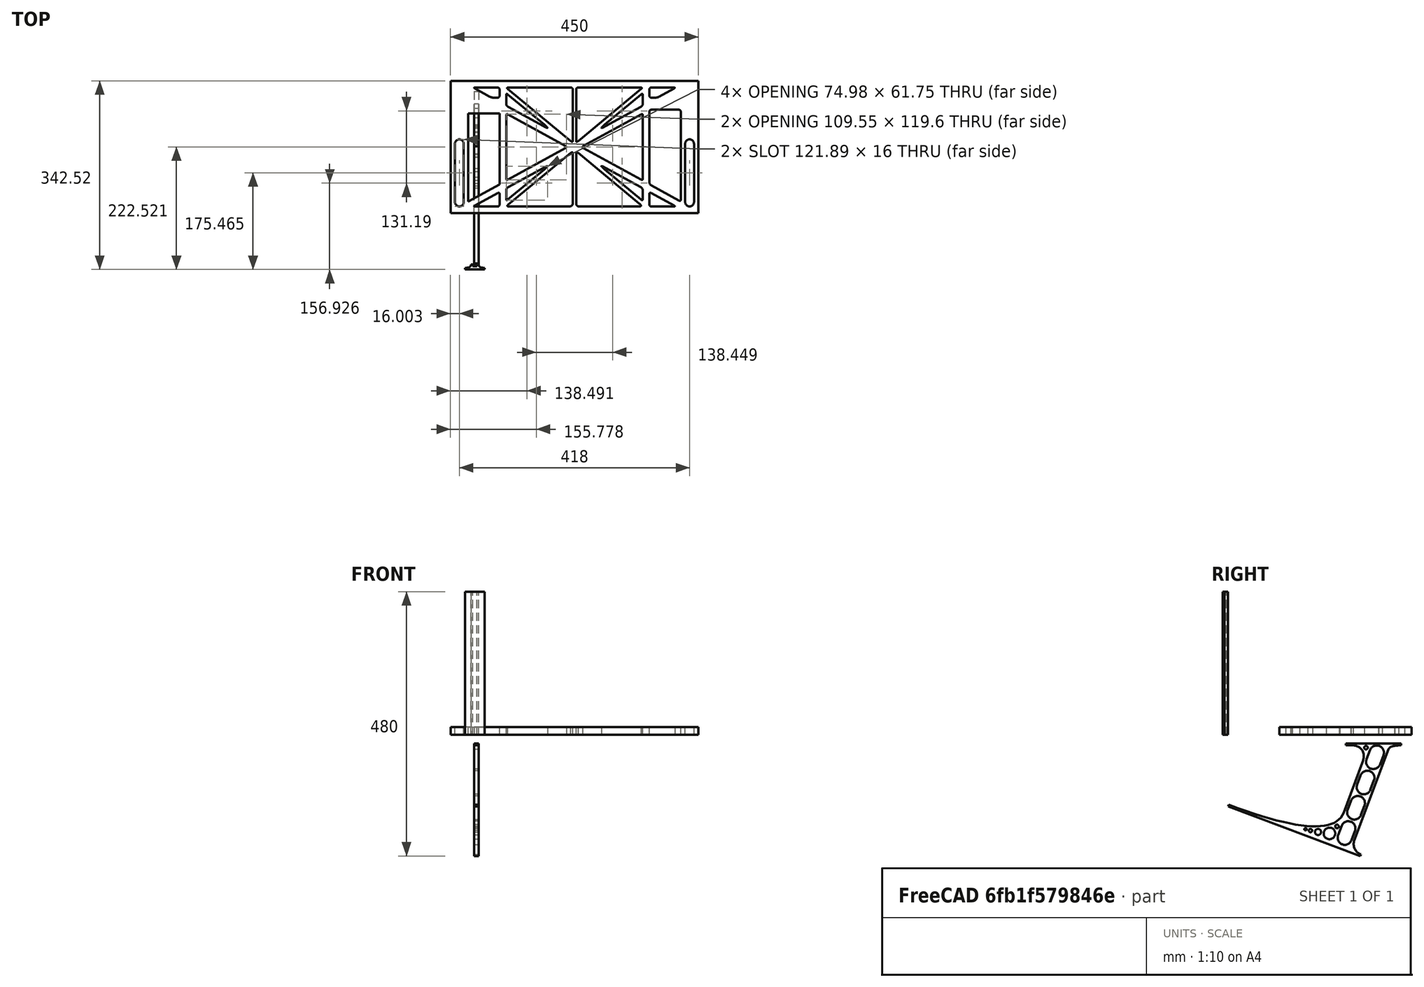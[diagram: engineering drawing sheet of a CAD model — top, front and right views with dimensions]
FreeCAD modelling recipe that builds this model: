
FCSTD DOCUMENT  (FreeCAD 0.19R0.19.2)
Label: laptopStand126FCStd
License: All rights reserved
LicenseURL: http://en.wikipedia.org/wiki/All_rights_reserved
objects: Sketcher::SketchObject×3, Part::Extrusion×3
note: 6 computed .brp shape members not serialized (recipe doc carries the construction recipe); baked Part::Feature solids carry a one-line shape summary decoded from their .brp

FEATURE [Sketcher::SketchObject] Sketch
  FullyConstrained = false
  sketch-geometry (352):
    g0: LineSegment StartX=-10.9272 StartY=-82.7794 StartZ=0 EndX=46.0728 EndY=-51.4823 EndZ=0
    g1: LineSegment StartX=-10.9272 StartY=76.4095 StartZ=0 EndX=-10.9272 EndY=-82.7794 EndZ=0
    g2: LineSegment StartX=46.0728 StartY=76.4095 StartZ=0 EndX=46.0728 EndY=-51.4823 EndZ=0
    g3: LineSegment StartX=-42.9272 StartY=136.221 StartZ=0 EndX=-42.9272 EndY=-103.779 EndZ=0
    g4: LineSegment StartX=407.073 StartY=136.221 StartZ=0 EndX=407.073 EndY=-103.779 EndZ=0
    g5: ArcOfCircle CenterX=-26.9272 CenterY=22.1087 CenterZ=0 NormalX=0 NormalY=0 NormalZ=1 AngleXU=0 Radius=8 StartAngle=1e-16 EndAngle=3.14159
    g6: ArcOfCircle CenterX=-26.9272 CenterY=-83.7794 CenterZ=0 NormalX=0 NormalY=0 NormalZ=1 AngleXU=0 Radius=8 StartAngle=3.14159 EndAngle=6.28319
    g7: LineSegment StartX=-34.9272 StartY=22.1087 StartZ=0 EndX=-34.9272 EndY=-83.7794 EndZ=0
    g8: LineSegment StartX=-18.9272 StartY=22.1087 StartZ=0 EndX=-18.9272 EndY=-83.7794 EndZ=0
    g9: ArcOfCircle CenterX=391.073 CenterY=22.1087 CenterZ=0 NormalX=0 NormalY=0 NormalZ=1 AngleXU=0 Radius=8 StartAngle=-4.4e-15 EndAngle=3.14159
    g10: LineSegment StartX=399.073 StartY=22.1087 StartZ=0 EndX=399.073 EndY=-83.7794 EndZ=0
    g11: LineSegment StartX=383.073 StartY=22.1087 StartZ=0 EndX=383.073 EndY=-83.7794 EndZ=0
    g12: ArcOfCircle CenterX=391.073 CenterY=-83.7794 CenterZ=0 NormalX=0 NormalY=0 NormalZ=1 AngleXU=0 Radius=8 StartAngle=3.14159 EndAngle=6.28319
    g13: Circle CenterX=175.022 CenterY=27.0628 CenterZ=0 NormalX=0 NormalY=0 NormalZ=1 AngleXU=0 Radius=1
    g14: Circle CenterX=179.022 CenterY=24.8665 CenterZ=0 NormalX=0 NormalY=0 NormalZ=1 AngleXU=0 Radius=1
    g15: Circle CenterX=179.022 CenterY=27.0628 CenterZ=0 NormalX=0 NormalY=0 NormalZ=1 AngleXU=0 Radius=1
    g16: BSplineCurve PolesCount=3 KnotsCount=2 Degree=2 IsPeriodic=0
    g17: GeomPoint X=175.022 Y=27.0628 Z=0
    g18: GeomPoint X=179.022 Y=27.0628 Z=0
    g19: Circle CenterX=189.124 CenterY=27.0628 CenterZ=0 NormalX=0 NormalY=0 NormalZ=1 AngleXU=0 Radius=1
    g20: Circle CenterX=185.124 CenterY=24.8665 CenterZ=0 NormalX=0 NormalY=0 NormalZ=1 AngleXU=0 Radius=1
    g21: Circle CenterX=185.124 CenterY=27.0628 CenterZ=0 NormalX=0 NormalY=0 NormalZ=1 AngleXU=0 Radius=1
    g22: BSplineCurve PolesCount=3 KnotsCount=2 Degree=2 IsPeriodic=0
    g23: GeomPoint X=189.124 Y=27.0628 Z=0
    g24: GeomPoint X=185.124 Y=27.0628 Z=0
    g25: Circle CenterX=175.022 CenterY=5.37834 CenterZ=0 NormalX=0 NormalY=0 NormalZ=1 AngleXU=0 Radius=1
    g26: Circle CenterX=179.022 CenterY=7.57463 CenterZ=0 NormalX=0 NormalY=0 NormalZ=1 AngleXU=0 Radius=1
    g27: Circle CenterX=179.022 CenterY=5.34704 CenterZ=0 NormalX=0 NormalY=0 NormalZ=1 AngleXU=0 Radius=1
    g28: BSplineCurve PolesCount=3 KnotsCount=2 Degree=2 IsPeriodic=0
    g29: GeomPoint X=175.022 Y=5.37834 Z=0
    g30: GeomPoint X=179.022 Y=5.34704 Z=0
    g31: Circle CenterX=189.124 CenterY=5.37834 CenterZ=0 NormalX=0 NormalY=0 NormalZ=1 AngleXU=0 Radius=1
    g32: Circle CenterX=185.124 CenterY=7.57463 CenterZ=0 NormalX=0 NormalY=0 NormalZ=1 AngleXU=0 Radius=1
    g33: Circle CenterX=185.124 CenterY=5.34704 CenterZ=0 NormalX=0 NormalY=0 NormalZ=1 AngleXU=0 Radius=1
    g34: BSplineCurve PolesCount=3 KnotsCount=2 Degree=2 IsPeriodic=0
    g35: GeomPoint X=189.124 Y=5.37834 Z=0
    g36: GeomPoint X=185.124 Y=5.34704 Z=0
    g37: Circle CenterX=165.871 CenterY=18.1458 CenterZ=0 NormalX=0 NormalY=0 NormalZ=1 AngleXU=0 Radius=1
    g38: Circle CenterX=169.377 CenterY=16.2206 CenterZ=0 NormalX=0 NormalY=0 NormalZ=1 AngleXU=0 Radius=1
    g39: Circle CenterX=165.871 CenterY=14.2954 CenterZ=0 NormalX=0 NormalY=0 NormalZ=1 AngleXU=0 Radius=1
    g40: BSplineCurve PolesCount=3 KnotsCount=2 Degree=2 IsPeriodic=0
    g41: GeomPoint X=165.871 Y=18.1458 Z=0
    g42: GeomPoint X=165.871 Y=14.2954 Z=0
    g43: Circle CenterX=198.275 CenterY=18.1458 CenterZ=0 NormalX=0 NormalY=0 NormalZ=1 AngleXU=0 Radius=1
    g44: Circle CenterX=194.768 CenterY=16.2206 CenterZ=0 NormalX=0 NormalY=0 NormalZ=1 AngleXU=0 Radius=1
    g45: Circle CenterX=198.275 CenterY=14.2954 CenterZ=0 NormalX=0 NormalY=0 NormalZ=1 AngleXU=0 Radius=1
    g46: BSplineCurve PolesCount=3 KnotsCount=2 Degree=2 IsPeriodic=0
    g47: GeomPoint X=198.275 Y=18.1458 Z=0
    g48: GeomPoint X=198.275 Y=14.2954 Z=0
    g49: LineSegment StartX=407.073 StartY=-103.779 StartZ=0 EndX=-42.9272 EndY=-103.779 EndZ=0
    g50: LineSegment StartX=407.073 StartY=136.221 StartZ=0 EndX=-42.9272 EndY=136.221 EndZ=0
    g51: LineSegment StartX=46.0728 StartY=76.4095 StartZ=0 EndX=-10.9272 EndY=76.4095 EndZ=0
    g52: Circle CenterX=125.607 CenterY=54.1951 CenterZ=0 NormalX=0 NormalY=0 NormalZ=1 AngleXU=0 Radius=1
    g53: Circle CenterX=139.632 CenterY=46.4944 CenterZ=0 NormalX=0 NormalY=0 NormalZ=1 AngleXU=0 Radius=1
    g54: Circle CenterX=127.326 CenterY=56.7187 CenterZ=0 NormalX=0 NormalY=0 NormalZ=1 AngleXU=0 Radius=1
    g55: BSplineCurve PolesCount=3 KnotsCount=2 Degree=2 IsPeriodic=0
    g56: GeomPoint X=125.607 Y=54.1951 Z=0
    g57: GeomPoint X=127.326 Y=56.7187 Z=0
    g58: Circle CenterX=236.821 CenterY=56.7187 CenterZ=0 NormalX=0 NormalY=0 NormalZ=1 AngleXU=0 Radius=1
    g59: Circle CenterX=224.513 CenterY=46.4944 CenterZ=0 NormalX=0 NormalY=0 NormalZ=1 AngleXU=0 Radius=1
    g60: Circle CenterX=238.538 CenterY=54.1951 CenterZ=0 NormalX=0 NormalY=0 NormalZ=1 AngleXU=0 Radius=1
    g61: BSplineCurve PolesCount=3 KnotsCount=2 Degree=2 IsPeriodic=0
    g62: GeomPoint X=236.821 Y=56.7187 Z=0
    g63: GeomPoint X=238.538 Y=54.1951 Z=0
    g64: Circle CenterX=238.538 CenterY=-21.7539 CenterZ=0 NormalX=0 NormalY=0 NormalZ=1 AngleXU=0 Radius=1
    g65: Circle CenterX=224.513 CenterY=-14.0532 CenterZ=0 NormalX=0 NormalY=0 NormalZ=1 AngleXU=0 Radius=1
    g66: Circle CenterX=236.821 CenterY=-24.2775 CenterZ=0 NormalX=0 NormalY=0 NormalZ=1 AngleXU=0 Radius=1
    g67: BSplineCurve PolesCount=3 KnotsCount=2 Degree=2 IsPeriodic=0
    g68: GeomPoint X=238.538 Y=-21.7539 Z=0
    g69: GeomPoint X=236.821 Y=-24.2775 Z=0
    g70: Circle CenterX=125.607 CenterY=-21.7539 CenterZ=0 NormalX=0 NormalY=0 NormalZ=1 AngleXU=0 Radius=1
    g71: Circle CenterX=139.632 CenterY=-14.0532 CenterZ=0 NormalX=0 NormalY=0 NormalZ=1 AngleXU=0 Radius=1
    g72: Circle CenterX=127.325 CenterY=-24.2775 CenterZ=0 NormalX=0 NormalY=0 NormalZ=1 AngleXU=0 Radius=1
    g73: BSplineCurve PolesCount=3 KnotsCount=2 Degree=2 IsPeriodic=0
    g74: GeomPoint X=125.607 Y=-21.7539 Z=0
    g75: GeomPoint X=127.325 Y=-24.2775 Z=0
    g76: Circle CenterX=302.996 CenterY=111.695 CenterZ=0 NormalX=0 NormalY=0 NormalZ=1 AngleXU=0 Radius=1
    g77: Circle CenterX=306.073 CenterY=114.251 CenterZ=0 NormalX=0 NormalY=0 NormalZ=1 AngleXU=0 Radius=1
    g78: Circle CenterX=306.073 CenterY=110.251 CenterZ=0 NormalX=0 NormalY=0 NormalZ=1 AngleXU=0 Radius=1
    g79: BSplineCurve PolesCount=3 KnotsCount=2 Degree=2 IsPeriodic=0
    g80: GeomPoint X=302.996 Y=111.695 Z=0
    g81: GeomPoint X=306.073 Y=110.251 Z=0
    g82: Circle CenterX=306.073 CenterY=95.2763 CenterZ=0 NormalX=0 NormalY=0 NormalZ=1 AngleXU=0 Radius=1
    g83: Circle CenterX=306.073 CenterY=91.2763 CenterZ=0 NormalX=0 NormalY=0 NormalZ=1 AngleXU=0 Radius=1
    g84: Circle CenterX=302.567 CenterY=89.3511 CenterZ=0 NormalX=0 NormalY=0 NormalZ=1 AngleXU=0 Radius=1
    g85: BSplineCurve PolesCount=3 KnotsCount=2 Degree=2 IsPeriodic=0
    g86: GeomPoint X=306.073 Y=95.2763 Z=0
    g87: GeomPoint X=302.567 Y=89.3511 Z=0
    g88: LineSegment StartX=306.073 StartY=110.251 StartZ=0 EndX=306.073 EndY=95.2763 EndZ=0
    g89: LineSegment StartX=302.996 StartY=111.695 StartZ=0 EndX=236.821 EndY=56.7187 EndZ=0
    g90: LineSegment StartX=238.538 StartY=54.1951 StartZ=0 EndX=302.567 EndY=89.3511 EndZ=0
    g91: Circle CenterX=61.1496 CenterY=111.695 CenterZ=0 NormalX=0 NormalY=0 NormalZ=1 AngleXU=0 Radius=1
    g92: Circle CenterX=58.0728 CenterY=114.251 CenterZ=0 NormalX=0 NormalY=0 NormalZ=1 AngleXU=0 Radius=1
    g93: Circle CenterX=58.0728 CenterY=110.251 CenterZ=0 NormalX=0 NormalY=0 NormalZ=1 AngleXU=0 Radius=1
    g94: BSplineCurve PolesCount=3 KnotsCount=2 Degree=2 IsPeriodic=0
    g95: GeomPoint X=61.1496 Y=111.695 Z=0
    g96: GeomPoint X=58.0728 Y=110.251 Z=0
    g97: Circle CenterX=61.5791 CenterY=89.3511 CenterZ=0 NormalX=0 NormalY=0 NormalZ=1 AngleXU=0 Radius=1
    g98: Circle CenterX=58.0728 CenterY=91.2763 CenterZ=0 NormalX=0 NormalY=0 NormalZ=1 AngleXU=0 Radius=1
    g99: Circle CenterX=58.0728 CenterY=95.2763 CenterZ=0 NormalX=0 NormalY=0 NormalZ=1 AngleXU=0 Radius=1
    g100: BSplineCurve PolesCount=3 KnotsCount=2 Degree=2 IsPeriodic=0
    g101: GeomPoint X=61.5791 Y=89.3511 Z=0
    g102: GeomPoint X=58.0728 Y=95.2763 Z=0
    g103: LineSegment StartX=58.0728 StartY=110.251 StartZ=0 EndX=58.0728 EndY=95.2763 EndZ=0
    g104: LineSegment StartX=61.1496 StartY=111.695 StartZ=0 EndX=127.326 EndY=56.7187 EndZ=0
    g105: LineSegment StartX=125.607 StartY=54.1951 StartZ=0 EndX=61.5791 EndY=89.3511 EndZ=0
    g106: Circle CenterX=61.5791 CenterY=-56.9099 CenterZ=0 NormalX=0 NormalY=0 NormalZ=1 AngleXU=0 Radius=1
    g107: Circle CenterX=58.0728 CenterY=-58.8351 CenterZ=0 NormalX=0 NormalY=0 NormalZ=1 AngleXU=0 Radius=1
    g108: Circle CenterX=58.0728 CenterY=-62.8351 CenterZ=0 NormalX=0 NormalY=0 NormalZ=1 AngleXU=0 Radius=1
    g109: BSplineCurve PolesCount=3 KnotsCount=2 Degree=2 IsPeriodic=0
    g110: GeomPoint X=61.5791 Y=-56.9099 Z=0
    g111: GeomPoint X=58.0728 Y=-62.8351 Z=0
    g112: Circle CenterX=58.0728 CenterY=-77.8102 CenterZ=0 NormalX=0 NormalY=0 NormalZ=1 AngleXU=0 Radius=1
    g113: Circle CenterX=58.0728 CenterY=-81.8102 CenterZ=0 NormalX=0 NormalY=0 NormalZ=1 AngleXU=0 Radius=1
    g114: Circle CenterX=61.1496 CenterY=-79.2541 CenterZ=0 NormalX=0 NormalY=0 NormalZ=1 AngleXU=0 Radius=1
    g115: BSplineCurve PolesCount=3 KnotsCount=2 Degree=2 IsPeriodic=0
    g116: GeomPoint X=58.0728 Y=-77.8102 Z=0
    g117: GeomPoint X=61.1496 Y=-79.2541 Z=0
    g118: LineSegment StartX=58.0728 StartY=-62.8351 StartZ=0 EndX=58.0728 EndY=-77.8102 EndZ=0
    g119: LineSegment StartX=61.1496 StartY=-79.2541 StartZ=0 EndX=127.325 EndY=-24.2775 EndZ=0
    g120: LineSegment StartX=125.607 StartY=-21.7539 StartZ=0 EndX=61.5791 EndY=-56.9099 EndZ=0
    g121: Circle CenterX=302.567 CenterY=-56.9099 CenterZ=0 NormalX=0 NormalY=0 NormalZ=1 AngleXU=0 Radius=1
    g122: Circle CenterX=306.073 CenterY=-58.8351 CenterZ=0 NormalX=0 NormalY=0 NormalZ=1 AngleXU=0 Radius=1
    g123: Circle CenterX=306.073 CenterY=-62.8351 CenterZ=0 NormalX=0 NormalY=0 NormalZ=1 AngleXU=0 Radius=1
    g124: BSplineCurve PolesCount=3 KnotsCount=2 Degree=2 IsPeriodic=0
    g125: GeomPoint X=302.567 Y=-56.9099 Z=0
    g126: GeomPoint X=306.073 Y=-62.8351 Z=0
    g127: Circle CenterX=302.996 CenterY=-79.2541 CenterZ=0 NormalX=0 NormalY=0 NormalZ=1 AngleXU=0 Radius=1
    g128: Circle CenterX=306.073 CenterY=-81.8102 CenterZ=0 NormalX=0 NormalY=0 NormalZ=1 AngleXU=0 Radius=1
    g129: Circle CenterX=306.073 CenterY=-77.8102 CenterZ=0 NormalX=0 NormalY=0 NormalZ=1 AngleXU=0 Radius=1
    g130: BSplineCurve PolesCount=3 KnotsCount=2 Degree=2 IsPeriodic=0
    g131: GeomPoint X=302.996 Y=-79.2541 Z=0
    g132: GeomPoint X=306.073 Y=-77.8102 Z=0
    g133: LineSegment StartX=306.073 StartY=-62.8351 StartZ=0 EndX=306.073 EndY=-77.8102 EndZ=0
    g134: LineSegment StartX=302.996 StartY=-79.2541 StartZ=0 EndX=236.821 EndY=-24.2775 EndZ=0
    g135: LineSegment StartX=238.538 StartY=-21.7539 StartZ=0 EndX=302.567 EndY=-56.9099 EndZ=0
    g136: Circle CenterX=61.6457 CenterY=-88.8112 CenterZ=0 NormalX=0 NormalY=0 NormalZ=1 AngleXU=0 Radius=1
    g137: Circle CenterX=58.0728 CenterY=-91.7794 CenterZ=0 NormalX=0 NormalY=0 NormalZ=1 AngleXU=0 Radius=1
    g138: Circle CenterX=63.9135 CenterY=-91.7794 CenterZ=0 NormalX=0 NormalY=0 NormalZ=1 AngleXU=0 Radius=1
    g139: BSplineCurve PolesCount=3 KnotsCount=2 Degree=2 IsPeriodic=0
    g140: GeomPoint X=61.6457 Y=-88.8112 Z=0
    g141: GeomPoint X=63.9135 Y=-91.7794 Z=0
    g142: Circle CenterX=179.022 CenterY=-85.8163 CenterZ=0 NormalX=0 NormalY=0 NormalZ=1 AngleXU=0 Radius=1
    g143: Circle CenterX=179.022 CenterY=-91.7794 CenterZ=0 NormalX=0 NormalY=0 NormalZ=1 AngleXU=0 Radius=1
    g144: Circle CenterX=171.895 CenterY=-91.7794 CenterZ=0 NormalX=0 NormalY=0 NormalZ=1 AngleXU=0 Radius=1
    g145: BSplineCurve PolesCount=3 KnotsCount=2 Degree=2 IsPeriodic=0
    g146: GeomPoint X=179.022 Y=-85.8163 Z=0
    g147: GeomPoint X=171.895 Y=-91.7794 Z=0
    g148: Circle CenterX=185.124 CenterY=-86.2028 CenterZ=0 NormalX=0 NormalY=0 NormalZ=1 AngleXU=0 Radius=1
    g149: Circle CenterX=185.124 CenterY=-91.7794 CenterZ=0 NormalX=0 NormalY=0 NormalZ=1 AngleXU=0 Radius=1
    g150: Circle CenterX=191.747 CenterY=-91.7794 CenterZ=0 NormalX=0 NormalY=0 NormalZ=1 AngleXU=0 Radius=1
    g151: BSplineCurve PolesCount=3 KnotsCount=2 Degree=2 IsPeriodic=0
    g152: GeomPoint X=185.124 Y=-86.2028 Z=0
    g153: GeomPoint X=191.747 Y=-91.7794 Z=0
    g154: Circle CenterX=299.888 CenterY=-86.6413 CenterZ=0 NormalX=0 NormalY=0 NormalZ=1 AngleXU=0 Radius=1
    g155: Circle CenterX=306.073 CenterY=-91.7794 CenterZ=0 NormalX=0 NormalY=0 NormalZ=1 AngleXU=0 Radius=1
    g156: Circle CenterX=298.776 CenterY=-91.7794 CenterZ=0 NormalX=0 NormalY=0 NormalZ=1 AngleXU=0 Radius=1
    g157: BSplineCurve PolesCount=3 KnotsCount=2 Degree=2 IsPeriodic=0
    g158: GeomPoint X=299.888 Y=-86.6413 Z=0
    g159: GeomPoint X=298.776 Y=-91.7794 Z=0
    g160: LineSegment StartX=189.124 StartY=5.37834 StartZ=0 EndX=299.888 EndY=-86.6413 EndZ=0
    g161: LineSegment StartX=298.776 StartY=-91.7794 StartZ=0 EndX=191.747 EndY=-91.7794 EndZ=0
    g162: LineSegment StartX=185.124 StartY=-86.2028 StartZ=0 EndX=185.124 EndY=5.34704 EndZ=0
    g163: LineSegment StartX=179.022 StartY=5.34704 StartZ=0 EndX=179.022 EndY=-85.8163 EndZ=0
    g164: LineSegment StartX=171.895 StartY=-91.7794 StartZ=0 EndX=63.9135 EndY=-91.7794 EndZ=0
    g165: LineSegment StartX=61.6457 StartY=-88.8112 StartZ=0 EndX=175.022 EndY=5.37834 EndZ=0
    g166: Circle CenterX=302.073 CenterY=124.221 CenterZ=0 NormalX=0 NormalY=0 NormalZ=1 AngleXU=0 Radius=1
    g167: Circle CenterX=306.073 CenterY=124.221 CenterZ=0 NormalX=0 NormalY=0 NormalZ=1 AngleXU=0 Radius=1
    g168: Circle CenterX=302.996 CenterY=121.665 CenterZ=0 NormalX=0 NormalY=0 NormalZ=1 AngleXU=0 Radius=1
    g169: BSplineCurve PolesCount=3 KnotsCount=2 Degree=2 IsPeriodic=0
    g170: GeomPoint X=302.073 Y=124.221 Z=0
    g171: GeomPoint X=302.996 Y=121.665 Z=0
    g172: Circle CenterX=189.124 CenterY=124.221 CenterZ=0 NormalX=0 NormalY=0 NormalZ=1 AngleXU=0 Radius=1
    g173: Circle CenterX=185.124 CenterY=124.221 CenterZ=0 NormalX=0 NormalY=0 NormalZ=1 AngleXU=0 Radius=1
    g174: Circle CenterX=185.124 CenterY=120.221 CenterZ=0 NormalX=0 NormalY=0 NormalZ=1 AngleXU=0 Radius=1
    g175: BSplineCurve PolesCount=3 KnotsCount=2 Degree=2 IsPeriodic=0
    g176: GeomPoint X=189.124 Y=124.221 Z=0
    g177: GeomPoint X=185.124 Y=120.221 Z=0
    g178: Circle CenterX=175.022 CenterY=124.221 CenterZ=0 NormalX=0 NormalY=0 NormalZ=1 AngleXU=0 Radius=1
    g179: Circle CenterX=179.022 CenterY=124.221 CenterZ=0 NormalX=0 NormalY=0 NormalZ=1 AngleXU=0 Radius=1
    g180: Circle CenterX=179.022 CenterY=120.221 CenterZ=0 NormalX=0 NormalY=0 NormalZ=1 AngleXU=0 Radius=1
    g181: BSplineCurve PolesCount=3 KnotsCount=2 Degree=2 IsPeriodic=0
    g182: GeomPoint X=175.022 Y=124.221 Z=0
    g183: GeomPoint X=179.022 Y=120.221 Z=0
    g184: Circle CenterX=62.0728 CenterY=124.221 CenterZ=0 NormalX=0 NormalY=0 NormalZ=1 AngleXU=0 Radius=1
    g185: Circle CenterX=58.0728 CenterY=124.221 CenterZ=0 NormalX=0 NormalY=0 NormalZ=1 AngleXU=0 Radius=1
    g186: Circle CenterX=61.1496 CenterY=121.665 CenterZ=0 NormalX=0 NormalY=0 NormalZ=1 AngleXU=0 Radius=1
    g187: BSplineCurve PolesCount=3 KnotsCount=2 Degree=2 IsPeriodic=0
    g188: GeomPoint X=62.0728 Y=124.221 Z=0
    g189: GeomPoint X=61.1496 Y=121.665 Z=0
    g190: LineSegment StartX=62.0728 StartY=124.221 StartZ=0 EndX=175.022 EndY=124.221 EndZ=0
    g191: LineSegment StartX=179.022 StartY=120.221 StartZ=0 EndX=179.022 EndY=27.0628 EndZ=0
    g192: LineSegment StartX=185.124 StartY=27.0628 StartZ=0 EndX=185.124 EndY=120.221 EndZ=0
    g193: LineSegment StartX=189.124 StartY=124.221 StartZ=0 EndX=302.073 EndY=124.221 EndZ=0
    g194: LineSegment StartX=302.996 StartY=121.665 StartZ=0 EndX=189.124 EndY=27.0628 EndZ=0
    g195: LineSegment StartX=175.022 StartY=27.0628 StartZ=0 EndX=61.1496 EndY=121.665 EndZ=0
    g196: Circle CenterX=61.5791 CenterY=75.4095 CenterZ=0 NormalX=0 NormalY=0 NormalZ=1 AngleXU=0 Radius=1
    g197: Circle CenterX=58.0728 CenterY=77.3346 CenterZ=0 NormalX=0 NormalY=0 NormalZ=1 AngleXU=0 Radius=1
    g198: Circle CenterX=58.0728 CenterY=73.3346 CenterZ=0 NormalX=0 NormalY=0 NormalZ=1 AngleXU=0 Radius=1
    g199: BSplineCurve PolesCount=3 KnotsCount=2 Degree=2 IsPeriodic=0
    g200: GeomPoint X=61.5791 Y=75.4095 Z=0
    g201: GeomPoint X=58.0728 Y=73.3346 Z=0
    g202: Circle CenterX=58.0728 CenterY=-40.8935 CenterZ=0 NormalX=0 NormalY=0 NormalZ=1 AngleXU=0 Radius=1
    g203: Circle CenterX=58.0728 CenterY=-44.8935 CenterZ=0 NormalX=0 NormalY=0 NormalZ=1 AngleXU=0 Radius=1
    g204: Circle CenterX=61.5791 CenterY=-42.9683 CenterZ=0 NormalX=0 NormalY=0 NormalZ=1 AngleXU=0 Radius=1
    g205: BSplineCurve PolesCount=3 KnotsCount=2 Degree=2 IsPeriodic=0
    g206: GeomPoint X=58.0728 Y=-40.8935 Z=0
    g207: GeomPoint X=61.5791 Y=-42.9683 Z=0
    g208: LineSegment StartX=61.5791 StartY=-42.9683 StartZ=0 EndX=165.871 EndY=14.2954 EndZ=0
    g209: LineSegment StartX=165.871 StartY=18.1458 StartZ=0 EndX=61.5791 EndY=75.4095 EndZ=0
    g210: LineSegment StartX=58.0728 StartY=73.3346 StartZ=0 EndX=58.0728 EndY=-40.8935 EndZ=0
    g211: Circle CenterX=302.567 CenterY=-42.9683 CenterZ=0 NormalX=0 NormalY=0 NormalZ=1 AngleXU=0 Radius=1
    g212: Circle CenterX=306.073 CenterY=-44.8935 CenterZ=0 NormalX=0 NormalY=0 NormalZ=1 AngleXU=0 Radius=1
    g213: Circle CenterX=306.073 CenterY=-40.8935 CenterZ=0 NormalX=0 NormalY=0 NormalZ=1 AngleXU=0 Radius=1
    g214: BSplineCurve PolesCount=3 KnotsCount=2 Degree=2 IsPeriodic=0
    g215: GeomPoint X=302.567 Y=-42.9683 Z=0
    g216: GeomPoint X=306.073 Y=-40.8935 Z=0
    g217: Circle CenterX=306.073 CenterY=73.3346 CenterZ=0 NormalX=0 NormalY=0 NormalZ=1 AngleXU=0 Radius=1
    g218: Circle CenterX=306.073 CenterY=77.3346 CenterZ=0 NormalX=0 NormalY=0 NormalZ=1 AngleXU=0 Radius=1
    g219: Circle CenterX=302.567 CenterY=75.4095 CenterZ=0 NormalX=0 NormalY=0 NormalZ=1 AngleXU=0 Radius=1
    g220: BSplineCurve PolesCount=3 KnotsCount=2 Degree=2 IsPeriodic=0
    g221: GeomPoint X=306.073 Y=73.3346 Z=0
    g222: GeomPoint X=302.567 Y=75.4095 Z=0
    g223: LineSegment StartX=302.567 StartY=-42.9683 StartZ=0 EndX=198.275 EndY=14.2954 EndZ=0
    g224: LineSegment StartX=198.275 StartY=18.1458 StartZ=0 EndX=302.567 EndY=75.4095 EndZ=0
    g225: LineSegment StartX=306.073 StartY=73.3346 StartZ=0 EndX=306.073 EndY=-40.8935 EndZ=0
    g226: LineSegment StartX=322.073 StartY=105.865 StartZ=0 EndX=328.643 EndY=105.865 EndZ=0
    g227: LineSegment StartX=318.073 StartY=120.221 StartZ=0 EndX=318.073 EndY=109.865 EndZ=0
    g228: LineSegment StartX=336.157 StartY=107.779 StartZ=0 EndX=362.567 EndY=122.294 EndZ=0
    g229: Circle CenterX=362.073 CenterY=124.221 CenterZ=0 NormalX=0 NormalY=0 NormalZ=1 AngleXU=0 Radius=1
    g230: Circle CenterX=366.073 CenterY=124.221 CenterZ=0 NormalX=0 NormalY=0 NormalZ=1 AngleXU=0 Radius=1
    g231: Circle CenterX=362.567 CenterY=122.294 CenterZ=0 NormalX=0 NormalY=0 NormalZ=1 AngleXU=0 Radius=1
    g232: BSplineCurve PolesCount=3 KnotsCount=2 Degree=2 IsPeriodic=0
    g233: GeomPoint X=362.073 Y=124.221 Z=0
    g234: GeomPoint X=362.567 Y=122.294 Z=0
    g235: Circle CenterX=322.073 CenterY=124.221 CenterZ=0 NormalX=0 NormalY=0 NormalZ=1 AngleXU=0 Radius=1
    g236: Circle CenterX=318.073 CenterY=124.221 CenterZ=0 NormalX=0 NormalY=0 NormalZ=1 AngleXU=0 Radius=1
    g237: Circle CenterX=318.073 CenterY=120.221 CenterZ=0 NormalX=0 NormalY=0 NormalZ=1 AngleXU=0 Radius=1
    g238: BSplineCurve PolesCount=3 KnotsCount=2 Degree=2 IsPeriodic=0
    g239: GeomPoint X=322.073 Y=124.221 Z=0
    g240: GeomPoint X=318.073 Y=120.221 Z=0
    g241: Circle CenterX=322.073 CenterY=105.865 CenterZ=0 NormalX=0 NormalY=0 NormalZ=1 AngleXU=0 Radius=1
    g242: Circle CenterX=318.073 CenterY=105.865 CenterZ=0 NormalX=0 NormalY=0 NormalZ=1 AngleXU=0 Radius=1
    g243: Circle CenterX=318.073 CenterY=109.865 CenterZ=0 NormalX=0 NormalY=0 NormalZ=1 AngleXU=0 Radius=1
    g244: BSplineCurve PolesCount=3 KnotsCount=2 Degree=2 IsPeriodic=0
    g245: GeomPoint X=322.073 Y=105.865 Z=0
    g246: GeomPoint X=318.073 Y=109.865 Z=0
    g247: Circle CenterX=336.157 CenterY=107.779 CenterZ=0 NormalX=0 NormalY=0 NormalZ=1 AngleXU=0 Radius=1
    g248: Circle CenterX=332.651 CenterY=105.853 CenterZ=0 NormalX=0 NormalY=0 NormalZ=1 AngleXU=0 Radius=1
    g249: Circle CenterX=328.643 CenterY=105.865 CenterZ=0 NormalX=0 NormalY=0 NormalZ=1 AngleXU=0 Radius=1
    g250: BSplineCurve PolesCount=3 KnotsCount=2 Degree=2 IsPeriodic=0
    g251: GeomPoint X=336.157 Y=107.779 Z=0
    g252: GeomPoint X=328.643 Y=105.865 Z=0
    g253: LineSegment StartX=322.073 StartY=124.221 StartZ=0 EndX=362.073 EndY=124.221 EndZ=0
    g254: Circle CenterX=371.567 CenterY=-80.8644 CenterZ=0 NormalX=0 NormalY=0 NormalZ=1 AngleXU=0 Radius=1
    g255: Circle CenterX=375.073 CenterY=-82.7896 CenterZ=0 NormalX=0 NormalY=0 NormalZ=1 AngleXU=0 Radius=1
    g256: Circle CenterX=375.073 CenterY=-78.7896 CenterZ=0 NormalX=0 NormalY=0 NormalZ=1 AngleXU=0 Radius=1
    g257: BSplineCurve PolesCount=3 KnotsCount=2 Degree=2 IsPeriodic=0
    g258: GeomPoint X=371.567 Y=-80.8644 Z=0
    g259: GeomPoint X=375.073 Y=-78.7896 Z=0
    g260: Circle CenterX=321.579 CenterY=-53.4075 CenterZ=0 NormalX=0 NormalY=0 NormalZ=1 AngleXU=0 Radius=1
    g261: Circle CenterX=318.073 CenterY=-51.4823 CenterZ=0 NormalX=0 NormalY=0 NormalZ=1 AngleXU=0 Radius=1
    g262: Circle CenterX=318.073 CenterY=-47.4823 CenterZ=0 NormalX=0 NormalY=0 NormalZ=1 AngleXU=0 Radius=1
    g263: BSplineCurve PolesCount=3 KnotsCount=2 Degree=2 IsPeriodic=0
    g264: GeomPoint X=321.579 Y=-53.4075 Z=0
    g265: GeomPoint X=318.073 Y=-47.4823 Z=0
    g266: Circle CenterX=318.073 CenterY=79.9235 CenterZ=0 NormalX=0 NormalY=0 NormalZ=1 AngleXU=0 Radius=1
    g267: Circle CenterX=318.073 CenterY=83.9235 CenterZ=0 NormalX=0 NormalY=0 NormalZ=1 AngleXU=0 Radius=1
    g268: Circle CenterX=322.073 CenterY=83.9235 CenterZ=0 NormalX=0 NormalY=0 NormalZ=1 AngleXU=0 Radius=1
    g269: BSplineCurve PolesCount=3 KnotsCount=2 Degree=2 IsPeriodic=0
    g270: GeomPoint X=318.073 Y=79.9235 Z=0
    g271: GeomPoint X=322.073 Y=83.9235 Z=0
    g272: Circle CenterX=375.073 CenterY=79.9235 CenterZ=0 NormalX=0 NormalY=0 NormalZ=1 AngleXU=0 Radius=1
    g273: Circle CenterX=375.073 CenterY=83.9235 CenterZ=0 NormalX=0 NormalY=0 NormalZ=1 AngleXU=0 Radius=1
    g274: Circle CenterX=371.073 CenterY=83.9235 CenterZ=0 NormalX=0 NormalY=0 NormalZ=1 AngleXU=0 Radius=1
    g275: BSplineCurve PolesCount=3 KnotsCount=2 Degree=2 IsPeriodic=0
    g276: GeomPoint X=375.073 Y=79.9235 Z=0
    g277: GeomPoint X=371.073 Y=83.9235 Z=0
    g278: LineSegment StartX=322.073 StartY=83.9235 StartZ=0 EndX=371.073 EndY=83.9235 EndZ=0
    g279: LineSegment StartX=375.073 StartY=79.9235 StartZ=0 EndX=375.073 EndY=-78.7896 EndZ=0
    g280: LineSegment StartX=371.567 StartY=-80.8644 StartZ=0 EndX=321.579 EndY=-53.4075 EndZ=0
    g281: LineSegment StartX=318.073 StartY=-47.4823 StartZ=0 EndX=318.073 EndY=79.9235 EndZ=0
    g282: Circle CenterX=321.579 CenterY=-67.3492 CenterZ=0 NormalX=0 NormalY=0 NormalZ=1 AngleXU=0 Radius=1
    g283: Circle CenterX=318.073 CenterY=-65.424 CenterZ=0 NormalX=0 NormalY=0 NormalZ=1 AngleXU=0 Radius=1
    g284: Circle CenterX=318.073 CenterY=-69.424 CenterZ=0 NormalX=0 NormalY=0 NormalZ=1 AngleXU=0 Radius=1
    g285: BSplineCurve PolesCount=3 KnotsCount=2 Degree=2 IsPeriodic=0
    g286: GeomPoint X=321.579 Y=-67.3492 Z=0
    g287: GeomPoint X=318.073 Y=-69.424 Z=0
    g288: Circle CenterX=362.567 CenterY=-89.8542 CenterZ=0 NormalX=0 NormalY=0 NormalZ=1 AngleXU=0 Radius=1
    g289: Circle CenterX=366.073 CenterY=-91.7794 CenterZ=0 NormalX=0 NormalY=0 NormalZ=1 AngleXU=0 Radius=1
    g290: Circle CenterX=362.073 CenterY=-91.7794 CenterZ=0 NormalX=0 NormalY=0 NormalZ=1 AngleXU=0 Radius=1
    g291: BSplineCurve PolesCount=3 KnotsCount=2 Degree=2 IsPeriodic=0
    g292: GeomPoint X=362.567 Y=-89.8542 Z=0
    g293: GeomPoint X=362.073 Y=-91.7794 Z=0
    g294: Circle CenterX=322.073 CenterY=-91.7794 CenterZ=0 NormalX=0 NormalY=0 NormalZ=1 AngleXU=0 Radius=1
    g295: Circle CenterX=318.073 CenterY=-91.7794 CenterZ=0 NormalX=0 NormalY=0 NormalZ=1 AngleXU=0 Radius=1
    g296: Circle CenterX=318.073 CenterY=-87.7794 CenterZ=0 NormalX=0 NormalY=0 NormalZ=1 AngleXU=0 Radius=1
    g297: BSplineCurve PolesCount=3 KnotsCount=2 Degree=2 IsPeriodic=0
    g298: GeomPoint X=322.073 Y=-91.7794 Z=0
    g299: GeomPoint X=318.073 Y=-87.7794 Z=0
    g300: LineSegment StartX=362.567 StartY=-89.8542 StartZ=0 EndX=321.579 EndY=-67.3492 EndZ=0
    g301: LineSegment StartX=318.073 StartY=-69.424 StartZ=0 EndX=318.073 EndY=-87.7794 EndZ=0
    g302: LineSegment StartX=322.073 StartY=-91.7794 StartZ=0 EndX=362.073 EndY=-91.7794 EndZ=0
    g303: Circle CenterX=2.07281 CenterY=124.221 CenterZ=0 NormalX=0 NormalY=0 NormalZ=1 AngleXU=0 Radius=1
    g304: Circle CenterX=1.57905 CenterY=122.295 CenterZ=0 NormalX=0 NormalY=0 NormalZ=1 AngleXU=0 Radius=1
    g305: BSplineCurve PolesCount=3 KnotsCount=2 Degree=2 IsPeriodic=0
    g306: GeomPoint X=2.07281 Y=124.221 Z=0
    g307: GeomPoint X=1.57905 Y=122.295 Z=0
    g308: Circle CenterX=42.0728 CenterY=124.221 CenterZ=0 NormalX=0 NormalY=0 NormalZ=1 AngleXU=0 Radius=1
    g309: Circle CenterX=46.0728 CenterY=124.221 CenterZ=0 NormalX=0 NormalY=0 NormalZ=1 AngleXU=0 Radius=1
    g310: Circle CenterX=46.0728 CenterY=120.221 CenterZ=0 NormalX=0 NormalY=0 NormalZ=1 AngleXU=0 Radius=1
    g311: BSplineCurve PolesCount=3 KnotsCount=2 Degree=2 IsPeriodic=0
    g312: GeomPoint X=42.0728 Y=124.221 Z=0
    g313: GeomPoint X=46.0728 Y=120.221 Z=0
    g314: Circle CenterX=46.0728 CenterY=109.865 CenterZ=0 NormalX=0 NormalY=0 NormalZ=1 AngleXU=0 Radius=1
    g315: Circle CenterX=46.0728 CenterY=105.865 CenterZ=0 NormalX=0 NormalY=0 NormalZ=1 AngleXU=0 Radius=1
    g316: Circle CenterX=42.0728 CenterY=105.865 CenterZ=0 NormalX=0 NormalY=0 NormalZ=1 AngleXU=0 Radius=1
    g317: BSplineCurve PolesCount=3 KnotsCount=2 Degree=2 IsPeriodic=0
    g318: GeomPoint X=46.0728 Y=109.865 Z=0
    g319: GeomPoint X=42.0728 Y=105.865 Z=0
    g320: Circle CenterX=35.5028 CenterY=105.865 CenterZ=0 NormalX=0 NormalY=0 NormalZ=1 AngleXU=0 Radius=1
    g321: Circle CenterX=31.5028 CenterY=105.865 CenterZ=0 NormalX=0 NormalY=0 NormalZ=1 AngleXU=0 Radius=1
    g322: Circle CenterX=27.9965 CenterY=107.79 CenterZ=0 NormalX=0 NormalY=0 NormalZ=1 AngleXU=0 Radius=1
    g323: BSplineCurve PolesCount=3 KnotsCount=2 Degree=2 IsPeriodic=0
    g324: GeomPoint X=35.5028 Y=105.865 Z=0
    g325: GeomPoint X=27.9965 Y=107.79 Z=0
    g326: LineSegment StartX=2.07281 StartY=124.221 StartZ=0 EndX=42.0728 EndY=124.221 EndZ=0
    g327: LineSegment StartX=46.0728 StartY=120.221 StartZ=0 EndX=46.0728 EndY=109.865 EndZ=0
    g328: LineSegment StartX=42.0728 StartY=105.865 StartZ=0 EndX=35.5028 EndY=105.865 EndZ=0
    g329: LineSegment StartX=27.9965 StartY=107.79 StartZ=0 EndX=1.57905 EndY=122.295 EndZ=0
    g330: Circle CenterX=42.5666 CenterY=-67.3492 CenterZ=0 NormalX=0 NormalY=0 NormalZ=1 AngleXU=0 Radius=1
    g331: Circle CenterX=46.0728 CenterY=-65.424 CenterZ=0 NormalX=0 NormalY=0 NormalZ=1 AngleXU=0 Radius=1
    g332: Circle CenterX=46.0728 CenterY=-69.424 CenterZ=0 NormalX=0 NormalY=0 NormalZ=1 AngleXU=0 Radius=1
    g333: BSplineCurve PolesCount=3 KnotsCount=2 Degree=2 IsPeriodic=0
    g334: GeomPoint X=42.5666 Y=-67.3492 Z=0
    g335: GeomPoint X=46.0728 Y=-69.424 Z=0
    g336: Circle CenterX=46.0728 CenterY=-87.7794 CenterZ=0 NormalX=0 NormalY=0 NormalZ=1 AngleXU=0 Radius=1
    g337: Circle CenterX=46.0728 CenterY=-91.7794 CenterZ=0 NormalX=0 NormalY=0 NormalZ=1 AngleXU=0 Radius=1
    g338: Circle CenterX=42.0728 CenterY=-91.7794 CenterZ=0 NormalX=0 NormalY=0 NormalZ=1 AngleXU=0 Radius=1
    g339: BSplineCurve PolesCount=3 KnotsCount=2 Degree=2 IsPeriodic=0
    g340: GeomPoint X=46.0728 Y=-87.7794 Z=0
    g341: GeomPoint X=42.0728 Y=-91.7794 Z=0
    g342: Circle CenterX=2.07281 CenterY=-91.7794 CenterZ=0 NormalX=0 NormalY=0 NormalZ=1 AngleXU=0 Radius=1
    g343: Circle CenterX=-1.92719 CenterY=-91.7794 CenterZ=0 NormalX=0 NormalY=0 NormalZ=1 AngleXU=0 Radius=1
    g344: Circle CenterX=1.57905 CenterY=-89.8542 CenterZ=0 NormalX=0 NormalY=0 NormalZ=1 AngleXU=0 Radius=1
    g345: BSplineCurve PolesCount=3 KnotsCount=2 Degree=2 IsPeriodic=0
    g346: GeomPoint X=2.07281 Y=-91.7794 Z=0
    g347: GeomPoint X=1.57905 Y=-89.8542 Z=0
    g348: LineSegment StartX=2.07281 StartY=-91.7794 StartZ=0 EndX=42.0728 EndY=-91.7794 EndZ=0
    g349: LineSegment StartX=46.0728 StartY=-87.7794 StartZ=0 EndX=46.0728 EndY=-69.424 EndZ=0
    g350: LineSegment StartX=42.5666 StartY=-67.3492 StartZ=0 EndX=1.57905 EndY=-89.8542 EndZ=0
    g351: LineSegment StartX=46.0728 StartY=76.4095 StartZ=0 EndX=421.682 EndY=76.4095 EndZ=0
  constraints (585):
    c: Coincident(g0,g2)
    c: Block(g0)
    c: Block(g1)
    c: Vertical(g3)
    c: Vertical(g4)
    c: Block(g4)
    c: Block(g3)
    c: Tangent(g5,g8) = 1.5708
    c: Tangent(g5,g7) = -1.5708
    c: Tangent(g7,g6) = -1.5708
    c: Tangent(g8,g6) = 1.5708
    c: Vertical(g7)
    c: Equal(g5,g6)
    c: Block(g8)
    c: Block(g7)
    c: Tangent(g9,g10) = 1.5708
    c: Tangent(g10,g12) = 1.5708
    c: Equal(g9,g12)
    c: Coincident(g11,g9)
    c: Coincident(g11,g12)
    c: Block(g10)
    c: Block(g11)
    c: Weight(g13) = 1
    c: Equal(g13,g14)
    c: Equal(g13,g15)
    c: InternalAlignment(g13,g16)
    c: InternalAlignment(g14,g16)
    c: InternalAlignment(g15,g16)
    c: InternalAlignment(g17,g16)
    c: InternalAlignment(g18,g16)
    c: Weight(g19) = 1
    c: Equal(g19,g20)
    c: Equal(g19,g21)
    c: InternalAlignment(g19,g22)
    c: InternalAlignment(g20,g22)
    c: InternalAlignment(g21,g22)
    c: InternalAlignment(g23,g22)
    c: InternalAlignment(g24,g22)
    c: Block(g22)
    c: Block(g16)
    c: Weight(g25) = 1
    c: Equal(g25,g26)
    c: Equal(g25,g27)
    c: InternalAlignment(g25,g28)
    c: InternalAlignment(g26,g28)
    c: InternalAlignment(g27,g28)
    c: InternalAlignment(g29,g28)
    c: InternalAlignment(g30,g28)
    c: Weight(g31) = 1
    c: Equal(g31,g32)
    c: Equal(g31,g33)
    c: InternalAlignment(g31,g34)
    c: InternalAlignment(g32,g34)
    c: InternalAlignment(g33,g34)
    c: InternalAlignment(g35,g34)
    c: InternalAlignment(g36,g34)
    c: Block(g34)
    c: Block(g28)
    c: Weight(g37) = 1
    c: Equal(g37,g38)
    c: Equal(g37,g39)
    c: InternalAlignment(g37,g40)
    c: InternalAlignment(g38,g40)
    c: InternalAlignment(g39,g40)
    c: InternalAlignment(g41,g40)
    c: InternalAlignment(g42,g40)
    c: Weight(g43) = 1
    c: Equal(g43,g44)
    c: Equal(g43,g45)
    c: InternalAlignment(g43,g46)
    c: InternalAlignment(g44,g46)
    c: InternalAlignment(g45,g46)
    c: InternalAlignment(g47,g46)
    c: InternalAlignment(g48,g46)
    c: Block(g40)
    c: Block(g46)
    c: Coincident(g49,g4)
    c: Coincident(g49,g3)
    c: Horizontal(g49)
    c: Distance(g49) = 450
    c: Coincident(g50,g4)
    c: Coincident(g50,g3)
    c: Horizontal(g50)
    c: Horizontal(g51)
    c: Coincident(g2,g51)
    c: Block(g51)
    c: Coincident(g1,g51)
    c: Weight(g52) = 1
    c: Equal(g52,g53)
    c: Equal(g52,g54)
    c: InternalAlignment(g52,g55)
    c: InternalAlignment(g53,g55)
    c: InternalAlignment(g54,g55)
    c: InternalAlignment(g56,g55)
    c: InternalAlignment(g57,g55)
    c: Block(g55)
    c: Weight(g58) = 1
    c: Equal(g58,g59)
    c: Equal(g58,g60)
    c: InternalAlignment(g58,g61)
    c: InternalAlignment(g59,g61)
    c: InternalAlignment(g60,g61)
    c: InternalAlignment(g62,g61)
    c: InternalAlignment(g63,g61)
    c: Block(g61)
    c: Weight(g64) = 1
    c: Equal(g64,g65)
    c: Equal(g64,g66)
    c: InternalAlignment(g64,g67)
    c: InternalAlignment(g65,g67)
    c: InternalAlignment(g66,g67)
    c: InternalAlignment(g68,g67)
    c: InternalAlignment(g69,g67)
    c: Block(g67)
    c: Weight(g70) = 1
    c: Equal(g70,g71)
    c: Equal(g70,g72)
    c: InternalAlignment(g70,g73)
    c: InternalAlignment(g71,g73)
    c: InternalAlignment(g72,g73)
    c: InternalAlignment(g74,g73)
    c: InternalAlignment(g75,g73)
    c: Block(g73)
    c: Weight(g76) = 1
    c: Equal(g76,g77)
    c: Equal(g76,g78)
    c: InternalAlignment(g76,g79)
    c: InternalAlignment(g77,g79)
    c: InternalAlignment(g78,g79)
    c: InternalAlignment(g80,g79)
    c: InternalAlignment(g81,g79)
    c: Weight(g82) = 1
    c: Equal(g82,g83)
    c: Equal(g82,g84)
    c: InternalAlignment(g82,g85)
    c: InternalAlignment(g83,g85)
    c: InternalAlignment(g84,g85)
    c: InternalAlignment(g86,g85)
    c: InternalAlignment(g87,g85)
    c: Block(g79)
    c: Block(g85)
    c: Coincident(g88,g79)
    c: Coincident(g88,g85)
    c: Vertical(g88)
    c: Coincident(g89,g79)
    c: Coincident(g89,g61)
    c: Coincident(g90,g61)
    c: Coincident(g90,g85)
    c: Weight(g91) = 1
    c: Equal(g91,g92)
    c: Equal(g91,g93)
    c: InternalAlignment(g91,g94)
    c: InternalAlignment(g92,g94)
    c: InternalAlignment(g93,g94)
    c: InternalAlignment(g95,g94)
    c: InternalAlignment(g96,g94)
    c: Weight(g97) = 1
    c: Equal(g97,g98)
    c: Equal(g97,g99)
    c: InternalAlignment(g97,g100)
    c: InternalAlignment(g98,g100)
    c: InternalAlignment(g99,g100)
    c: InternalAlignment(g101,g100)
    c: InternalAlignment(g102,g100)
    c: Block(g94)
    c: Block(g100)
    c: Coincident(g103,g94)
    c: Coincident(g103,g100)
    c: Vertical(g103)
    c: Coincident(g104,g94)
    c: Coincident(g104,g55)
    c: Coincident(g105,g55)
    c: Coincident(g105,g100)
    c: Weight(g106) = 1
    c: Equal(g106,g107)
    c: Equal(g106,g108)
    c: InternalAlignment(g106,g109)
    c: InternalAlignment(g107,g109)
    c: InternalAlignment(g108,g109)
    c: InternalAlignment(g110,g109)
    c: InternalAlignment(g111,g109)
    c: Weight(g112) = 1
    c: Equal(g112,g113)
    c: Equal(g112,g114)
    c: InternalAlignment(g112,g115)
    c: InternalAlignment(g113,g115)
    c: InternalAlignment(g114,g115)
    c: InternalAlignment(g116,g115)
    c: InternalAlignment(g117,g115)
    c: Block(g109)
    c: Block(g115)
    c: Coincident(g118,g109)
    c: Coincident(g118,g115)
    c: Vertical(g118)
    c: Coincident(g119,g115)
    c: Coincident(g119,g73)
    c: Coincident(g120,g73)
    c: Coincident(g120,g109)
    c: Weight(g121) = 1
    c: Equal(g121,g122)
    c: Equal(g121,g123)
    c: InternalAlignment(g121,g124)
    c: InternalAlignment(g122,g124)
    c: InternalAlignment(g123,g124)
    c: InternalAlignment(g125,g124)
    c: InternalAlignment(g126,g124)
    c: Weight(g127) = 1
    c: Equal(g127,g128)
    c: Equal(g127,g129)
    c: InternalAlignment(g127,g130)
    c: InternalAlignment(g128,g130)
    c: InternalAlignment(g129,g130)
    c: InternalAlignment(g131,g130)
    c: InternalAlignment(g132,g130)
    c: Block(g124)
    c: Block(g130)
    c: Coincident(g133,g124)
    c: Coincident(g133,g130)
    c: Vertical(g133)
    c: Coincident(g134,g130)
    c: Coincident(g134,g67)
    c: Coincident(g135,g67)
    c: Coincident(g135,g124)
    c: Weight(g136) = 1
    c: Equal(g136,g137)
    c: Equal(g136,g138)
    c: InternalAlignment(g136,g139)
    c: InternalAlignment(g137,g139)
    c: InternalAlignment(g138,g139)
    c: InternalAlignment(g140,g139)
    c: InternalAlignment(g141,g139)
    c: Weight(g142) = 1
    c: Equal(g142,g143)
    c: Equal(g142,g144)
    c: InternalAlignment(g142,g145)
    c: InternalAlignment(g143,g145)
    c: InternalAlignment(g144,g145)
    c: InternalAlignment(g146,g145)
    c: InternalAlignment(g147,g145)
    c: Weight(g148) = 1
    c: Equal(g148,g149)
    c: Equal(g148,g150)
    c: InternalAlignment(g148,g151)
    c: InternalAlignment(g149,g151)
    c: InternalAlignment(g150,g151)
    c: InternalAlignment(g152,g151)
    c: InternalAlignment(g153,g151)
    c: Weight(g154) = 1
    c: Equal(g154,g155)
    c: Equal(g154,g156)
    c: InternalAlignment(g154,g157)
    c: InternalAlignment(g155,g157)
    c: InternalAlignment(g156,g157)
    c: InternalAlignment(g158,g157)
    c: InternalAlignment(g159,g157)
    c: Block(g157)
    c: Block(g151)
    c: Block(g145)
    c: Block(g139)
    c: Coincident(g160,g34)
    c: Coincident(g160,g157)
    c: Coincident(g161,g157)
    c: Coincident(g161,g151)
    c: Horizontal(g161)
    c: Coincident(g162,g151)
    c: Coincident(g162,g34)
    c: Vertical(g162)
    c: Coincident(g163,g28)
    c: Coincident(g163,g145)
    c: Vertical(g163)
    c: Coincident(g164,g145)
    c: Coincident(g164,g139)
    c: Horizontal(g164)
    c: Coincident(g165,g139)
    c: Coincident(g165,g28)
    c: Weight(g166) = 1
    c: Equal(g166,g167)
    c: Equal(g166,g168)
    c: InternalAlignment(g166,g169)
    c: InternalAlignment(g167,g169)
    c: InternalAlignment(g168,g169)
    c: InternalAlignment(g170,g169)
    c: InternalAlignment(g171,g169)
    c: Weight(g172) = 1
    c: Equal(g172,g173)
    c: Equal(g172,g174)
    c: InternalAlignment(g172,g175)
    c: InternalAlignment(g173,g175)
    c: InternalAlignment(g174,g175)
    c: InternalAlignment(g176,g175)
    c: InternalAlignment(g177,g175)
    c: Weight(g178) = 1
    c: Equal(g178,g179)
    c: Equal(g178,g180)
    c: InternalAlignment(g178,g181)
    c: InternalAlignment(g179,g181)
    c: InternalAlignment(g180,g181)
    c: InternalAlignment(g182,g181)
    c: InternalAlignment(g183,g181)
    c: Weight(g184) = 1
    c: Equal(g184,g185)
    c: Equal(g184,g186)
    c: InternalAlignment(g184,g187)
    c: InternalAlignment(g185,g187)
    c: InternalAlignment(g186,g187)
    c: InternalAlignment(g188,g187)
    c: InternalAlignment(g189,g187)
    c: Block(g187)
    c: Block(g181)
    c: Block(g175)
    c: Block(g169)
    c: Coincident(g190,g187)
    c: Coincident(g190,g181)
    c: Horizontal(g190)
    c: Coincident(g191,g181)
    c: Coincident(g191,g16)
    c: Vertical(g191)
    c: Coincident(g192,g22)
    c: Coincident(g192,g175)
    c: Vertical(g192)
    c: Coincident(g193,g175)
    c: Coincident(g193,g169)
    c: Horizontal(g193)
    c: Coincident(g194,g169)
    c: Coincident(g194,g22)
    c: Coincident(g195,g16)
    c: Weight(g196) = 1
    c: Equal(g196,g197)
    c: Equal(g196,g198)
    c: InternalAlignment(g196,g199)
    c: InternalAlignment(g197,g199)
    c: InternalAlignment(g198,g199)
    c: InternalAlignment(g200,g199)
    c: InternalAlignment(g201,g199)
    c: Weight(g202) = 1
    c: Equal(g202,g203)
    c: Equal(g202,g204)
    c: InternalAlignment(g202,g205)
    c: InternalAlignment(g203,g205)
    c: InternalAlignment(g204,g205)
    c: InternalAlignment(g206,g205)
    c: InternalAlignment(g207,g205)
    c: Block(g205)
    c: Block(g199)
    c: Coincident(g208,g205)
    c: Coincident(g208,g40)
    c: Coincident(g209,g40)
    c: Coincident(g209,g199)
    c: Coincident(g210,g199)
    c: Coincident(g210,g205)
    c: Vertical(g210)
    c: Weight(g211) = 1
    c: Equal(g211,g212)
    c: Equal(g211,g213)
    c: InternalAlignment(g211,g214)
    c: InternalAlignment(g212,g214)
    c: InternalAlignment(g213,g214)
    c: InternalAlignment(g215,g214)
    c: InternalAlignment(g216,g214)
    c: Weight(g217) = 1
    c: Equal(g217,g218)
    c: Equal(g217,g219)
    c: InternalAlignment(g217,g220)
    c: InternalAlignment(g218,g220)
    c: InternalAlignment(g219,g220)
    c: InternalAlignment(g221,g220)
    c: InternalAlignment(g222,g220)
    c: Block(g220)
    c: Block(g214)
    c: Coincident(g223,g214)
    c: Coincident(g223,g46)
    c: Coincident(g224,g46)
    c: Coincident(g224,g220)
    c: Coincident(g225,g220)
    c: Coincident(g225,g214)
    c: Vertical(g225)
    c: Horizontal(g226)
    c: Block(g226)
    c: Vertical(g227)
    c: Block(g227)
    c: Block(g228)
    c: Weight(g229) = 1
    c: Equal(g229,g230)
    c: Equal(g229,g231)
    c: InternalAlignment(g229,g232)
    c: InternalAlignment(g230,g232)
    c: InternalAlignment(g231,g232)
    c: InternalAlignment(g233,g232)
    c: InternalAlignment(g234,g232)
    c: Weight(g235) = 1
    c: Equal(g235,g236)
    c: Equal(g235,g237)
    c: InternalAlignment(g235,g238)
    c: InternalAlignment(g236,g238)
    c: InternalAlignment(g237,g238)
    c: InternalAlignment(g239,g238)
    c: InternalAlignment(g240,g238)
    c: Weight(g241) = 1
    c: Equal(g241,g242)
    c: Equal(g241,g243)
    c: InternalAlignment(g241,g244)
    c: InternalAlignment(g242,g244)
    c: InternalAlignment(g243,g244)
    c: InternalAlignment(g245,g244)
    c: InternalAlignment(g246,g244)
    c: Weight(g247) = 1
    c: Equal(g247,g248)
    c: Equal(g247,g249)
    c: InternalAlignment(g247,g250)
    c: InternalAlignment(g248,g250)
    c: InternalAlignment(g249,g250)
    c: InternalAlignment(g251,g250)
    c: InternalAlignment(g252,g250)
    c: Block(g232)
    c: Block(g238)
    c: Block(g244)
    c: Block(g250)
    c: Coincident(g253,g238)
    c: Coincident(g253,g232)
    c: Horizontal(g253)
    c: Block(g195)
    c: Weight(g254) = 1
    c: Equal(g254,g255)
    c: Equal(g254,g256)
    c: InternalAlignment(g254,g257)
    c: InternalAlignment(g255,g257)
    c: InternalAlignment(g256,g257)
    c: InternalAlignment(g258,g257)
    c: InternalAlignment(g259,g257)
    c: Weight(g260) = 1
    c: Equal(g260,g261)
    c: Equal(g260,g262)
    c: InternalAlignment(g260,g263)
    c: InternalAlignment(g261,g263)
    c: InternalAlignment(g262,g263)
    c: InternalAlignment(g264,g263)
    c: InternalAlignment(g265,g263)
    c: Weight(g266) = 1
    c: Equal(g266,g267)
    c: Equal(g266,g268)
    c: InternalAlignment(g266,g269)
    c: InternalAlignment(g267,g269)
    c: InternalAlignment(g268,g269)
    c: InternalAlignment(g270,g269)
    c: InternalAlignment(g271,g269)
    c: Weight(g272) = 1
    c: Equal(g272,g273)
    c: Equal(g272,g274)
    c: InternalAlignment(g272,g275)
    c: InternalAlignment(g273,g275)
    c: InternalAlignment(g274,g275)
    c: InternalAlignment(g276,g275)
    c: InternalAlignment(g277,g275)
    c: Block(g257)
    c: Block(g263)
    c: Block(g269)
    c: Block(g275)
    c: Coincident(g278,g269)
    c: Coincident(g278,g275)
    c: Horizontal(g278)
    c: Coincident(g279,g275)
    c: Coincident(g279,g257)
    c: Vertical(g279)
    c: Coincident(g280,g257)
    c: Coincident(g280,g263)
    c: Coincident(g281,g263)
    c: Coincident(g281,g269)
    c: Vertical(g281)
    c: Weight(g282) = 1
    c: Equal(g282,g283)
    c: Equal(g282,g284)
    c: InternalAlignment(g282,g285)
    c: InternalAlignment(g283,g285)
    c: InternalAlignment(g284,g285)
    c: InternalAlignment(g286,g285)
    c: InternalAlignment(g287,g285)
    c: Weight(g288) = 1
    c: Equal(g288,g289)
    c: Equal(g288,g290)
    c: InternalAlignment(g288,g291)
    c: InternalAlignment(g289,g291)
    c: InternalAlignment(g290,g291)
    c: InternalAlignment(g292,g291)
    c: InternalAlignment(g293,g291)
    c: Weight(g294) = 1
    c: Equal(g294,g295)
    c: Equal(g294,g296)
    c: InternalAlignment(g294,g297)
    c: InternalAlignment(g295,g297)
    c: InternalAlignment(g296,g297)
    c: InternalAlignment(g298,g297)
    c: InternalAlignment(g299,g297)
    c: Block(g297)
    c: Block(g291)
    c: Block(g285)
    c: Coincident(g300,g291)
    c: Coincident(g300,g285)
    c: Coincident(g301,g285)
    c: Coincident(g301,g297)
    c: Vertical(g301)
    c: Coincident(g302,g297)
    c: Coincident(g302,g291)
    c: Horizontal(g302)
    c: Weight(g303) = 1
    c: Equal(g303,g304)
    c: InternalAlignment(g303,g305)
    c: InternalAlignment(g304,g305)
    c: InternalAlignment(g306,g305)
    c: InternalAlignment(g307,g305)
    c: Weight(g308) = 1
    c: Equal(g308,g309)
    c: Equal(g308,g310)
    c: InternalAlignment(g308,g311)
    c: InternalAlignment(g309,g311)
    c: InternalAlignment(g310,g311)
    c: InternalAlignment(g312,g311)
    c: InternalAlignment(g313,g311)
    c: Weight(g314) = 1
    c: Equal(g314,g315)
    c: Equal(g314,g316)
    c: InternalAlignment(g314,g317)
    c: InternalAlignment(g315,g317)
    c: InternalAlignment(g316,g317)
    c: InternalAlignment(g318,g317)
    c: InternalAlignment(g319,g317)
    c: Equal(g320,g321)
    c: Equal(g320,g322)
    c: InternalAlignment(g320,g323)
    c: InternalAlignment(g321,g323)
    c: InternalAlignment(g322,g323)
    c: InternalAlignment(g324,g323)
    c: InternalAlignment(g325,g323)
    c: Block(g311)
    c: Block(g317)
    c: Block(g323)
    c: Block(g305)
    c: Coincident(g326,g305)
    c: Coincident(g326,g311)
    c: Horizontal(g326)
    c: Coincident(g327,g311)
    c: Coincident(g327,g317)
    c: Vertical(g327)
    c: Coincident(g328,g317)
    c: Coincident(g328,g323)
    c: Horizontal(g328)
    c: Coincident(g329,g323)
    c: Coincident(g329,g305)
    c: Weight(g330) = 1
    c: Equal(g330,g331)
    c: Equal(g330,g332)
    c: InternalAlignment(g330,g333)
    c: InternalAlignment(g331,g333)
    c: InternalAlignment(g332,g333)
    c: InternalAlignment(g334,g333)
    c: InternalAlignment(g335,g333)
    c: Weight(g336) = 1
    c: Equal(g336,g337)
    c: Equal(g336,g338)
    c: InternalAlignment(g336,g339)
    c: InternalAlignment(g337,g339)
    c: InternalAlignment(g338,g339)
    c: InternalAlignment(g340,g339)
    c: InternalAlignment(g341,g339)
    c: Weight(g342) = 1
    c: Equal(g342,g343)
    c: Equal(g342,g344)
    c: InternalAlignment(g342,g345)
    c: InternalAlignment(g343,g345)
    c: InternalAlignment(g344,g345)
    c: InternalAlignment(g346,g345)
    c: InternalAlignment(g347,g345)
    c: Block(g345)
    c: Block(g339)
    c: Block(g333)
    c: Coincident(g348,g345)
    c: Coincident(g348,g339)
    c: Horizontal(g348)
    c: Coincident(g349,g339)
    c: Coincident(g349,g333)
    c: Vertical(g349)
    c: Coincident(g350,g333)
    c: Coincident(g350,g345)
    c: Coincident(g351,g2)
    c: Horizontal(g351)
    c: Tangent(g351,g219)
FEATURE [Sketcher::SketchObject] Sketch001
  FullyConstrained = true
  MapMode = 4
  Placement = pos=(0,0,0) rot=(0.57735,0.57735,0.57735;2.0944rad)
  Support = -> [Sketch]
  sketch-geometry (46):
    g0: BSplineCurve PolesCount=3 KnotsCount=2 Degree=2 IsPeriodic=0
    g1: ArcOfCircle CenterX=73.1223 CenterY=-32.291 CenterZ=0 NormalX=0 NormalY=0 NormalZ=1 AngleXU=0 Radius=13 StartAngle=5.92268 EndAngle=9.06428
    g2: ArcOfCircle CenterX=66.7816 CenterY=-49.1439 CenterZ=0 NormalX=0 NormalY=0 NormalZ=1 AngleXU=0 Radius=13 StartAngle=2.78068 EndAngle=5.92131
    g3: ArcOfCircle CenterX=55.9263 CenterY=-78.1807 CenterZ=0 NormalX=0 NormalY=0 NormalZ=1 AngleXU=0 Radius=13 StartAngle=5.92268 EndAngle=9.06428
    g4: ArcOfCircle CenterX=49.5884 CenterY=-95.0342 CenterZ=0 NormalX=0 NormalY=0 NormalZ=1 AngleXU=0 Radius=13 StartAngle=2.78068 EndAngle=5.92131
    g5: ArcOfCircle CenterX=38.7206 CenterY=-124.067 CenterZ=0 NormalX=0 NormalY=0 NormalZ=1 AngleXU=0 Radius=13 StartAngle=5.92268 EndAngle=9.06428
    g6: ArcOfCircle CenterX=32.3875 CenterY=-140.92 CenterZ=0 NormalX=0 NormalY=0 NormalZ=1 AngleXU=0 Radius=13 StartAngle=2.78068 EndAngle=5.92131
    g7: ArcOfCircle CenterX=21.4715 CenterY=-169.934 CenterZ=0 NormalX=0 NormalY=0 NormalZ=1 AngleXU=0 Radius=13 StartAngle=5.92268 EndAngle=9.06428
    g8: ArcOfCircle CenterX=15.1336 CenterY=-186.787 CenterZ=0 NormalX=0 NormalY=0 NormalZ=1 AngleXU=0 Radius=13 StartAngle=2.78068 EndAngle=5.92131
    g9-g12: Circle x4 (B-spline internal-alignment scaffolding for g13; pole/knot coordinates omitted)
    g13: BSplineCurve PolesCount=4 KnotsCount=2 Degree=3 IsPeriodic=0
    g14: GeomPoint X=28.8094 Y=-19.0875 Z=0
    g15: GeomPoint X=47.0443 Y=-50.4712 Z=0
    g16: Circle CenterX=53.5586 CenterY=-23.2695 CenterZ=0 NormalX=0 NormalY=0 NormalZ=1 AngleXU=0 Radius=3.24518
    g17: Circle CenterX=-195.441 CenterY=-127.082 CenterZ=0 NormalX=0 NormalY=0 NormalZ=1 AngleXU=0 Radius=1
    g18: Circle CenterX=-8.24091 CenterY=-197.481 CenterZ=0 NormalX=0 NormalY=0 NormalZ=1 AngleXU=0 Radius=1
    g19: Circle CenterX=12.8789 CenterY=-141.321 CenterZ=0 NormalX=0 NormalY=0 NormalZ=1 AngleXU=0 Radius=1
    g20: BSplineCurve PolesCount=3 KnotsCount=2 Degree=2 IsPeriodic=0
    g21: GeomPoint X=-195.441 Y=-127.082 Z=0
    g22: GeomPoint X=12.8789 Y=-141.321 Z=0
    g23: Circle CenterX=-12.8016 CenterY=-179.036 CenterZ=0 NormalX=0 NormalY=0 NormalZ=1 AngleXU=0 Radius=10.5072
    g24: Circle CenterX=0.933922 CenterY=-166.43 CenterZ=0 NormalX=0 NormalY=0 NormalZ=1 AngleXU=0 Radius=3.26661
    g25: Circle CenterX=-33.5518 CenterY=-176.44 CenterZ=0 NormalX=0 NormalY=0 NormalZ=1 AngleXU=0 Radius=5.64388
    g26: Circle CenterX=-47.2366 CenterY=-173.859 CenterZ=0 NormalX=0 NormalY=0 NormalZ=1 AngleXU=0 Radius=3.01653
    g27: Circle CenterX=-56.2595 CenterY=-171.456 CenterZ=0 NormalX=0 NormalY=0 NormalZ=1 AngleXU=0 Radius=2.12826
    g28: ArcOfCircle CenterX=51.2151 CenterY=-198.473 CenterZ=0 NormalX=0 NormalY=0 NormalZ=1 AngleXU=0 Radius=20 StartAngle=2.78189 EndAngle=4.35269
    g29: LineSegment StartX=32.4951 StartY=-191.433 StartZ=0 EndX=94.6578 EndY=-26.1352 EndZ=0
    g30: LineSegment StartX=43.1192 StartY=-220.001 StartZ=0 EndX=-196.497 EndY=-129.89 EndZ=0
    g31: LineSegment StartX=43.1192 StartY=-220.001 StartZ=0 EndX=44.1752 EndY=-217.193 EndZ=0
    g32: LineSegment StartX=117.223 StartY=-19.0875 StartZ=0 EndX=117.223 EndY=-16.0875 EndZ=0
    g33: LineSegment StartX=117.223 StartY=-16.0875 StartZ=0 EndX=17.2232 EndY=-16.0875 EndZ=0
    g34: LineSegment StartX=17.2232 StartY=-16.0875 StartZ=0 EndX=17.2232 EndY=-19.0875 EndZ=0
    g35: LineSegment StartX=28.8094 StartY=-19.0875 StartZ=0 EndX=17.2232 EndY=-19.0875 EndZ=0
    g36: LineSegment StartX=47.0443 StartY=-50.4712 StartZ=0 EndX=12.8789 EndY=-141.321 EndZ=0
    g37: LineSegment StartX=-195.441 StartY=-127.082 StartZ=0 EndX=-196.497 EndY=-129.89 EndZ=0
    g38: LineSegment StartX=85.2866 StartY=-36.8766 StartZ=0 EndX=78.9396 EndY=-53.7463 EndZ=0
    g39: LineSegment StartX=60.9579 StartY=-27.7053 StartZ=0 EndX=54.6191 EndY=-44.5532 EndZ=0
    g40: LineSegment StartX=68.0907 StartY=-82.7664 StartZ=0 EndX=61.7465 EndY=-99.6365 EndZ=0
    g41: LineSegment StartX=43.7619 StartY=-73.595 StartZ=0 EndX=37.426 EndY=-90.4435 EndZ=0
    g42: LineSegment StartX=50.885 StartY=-128.652 StartZ=0 EndX=44.5456 EndY=-145.522 EndZ=0
    g43: LineSegment StartX=26.5562 StartY=-119.481 StartZ=0 EndX=20.2251 EndY=-136.329 EndZ=0
    g44: LineSegment StartX=9.3071 StartY=-165.349 StartZ=0 EndX=2.97115 EndY=-182.197 EndZ=0
    g45: LineSegment StartX=33.6358 StartY=-174.52 StartZ=0 EndX=27.2917 EndY=-191.39 EndZ=0
  constraints (71):
    c: Block(g0)
    c: Block(g1)
    c: Block(g2)
    c: Block(g4)
    c: Block(g3)
    c: Block(g6)
    c: Block(g5)
    c: Block(g8)
    c: Block(g7)
    c: Weight(g9) = 1
    c: Equal(g9,g10)
    c: Equal(g9,g11)
    c: Equal(g9,g12)
    c: InternalAlignment(g9-g12 -> g13) x4
    c: InternalAlignment(g14,g13)
    c: InternalAlignment(g15,g13)
    c: Block(g16)
    c: Weight(g17) = 1
    c: Equal(g17,g18)
    c: Equal(g17,g19)
    c: InternalAlignment(g17,g20)
    c: InternalAlignment(g18,g20)
    c: InternalAlignment(g19,g20)
    c: InternalAlignment(g21,g20)
    c: InternalAlignment(g22,g20)
    c: Block(g20)
    c: Block(g23)
    c: Block(g24)
    c: Block(g25)
    c: Block(g26)
    c: Block(g27)
    c: Block(g28)
    c: Coincident(g29,g28)
    c: Coincident(g29,g0)
    c: Block(g13)
    c: Coincident(g31,g30)
    c: Coincident(g31,g28)
    c: Block(g31)
    c: Coincident(g32,g0)
    c: Vertical(g32)
    c: Coincident(g33,g32)
    c: Horizontal(g33)
    c: Coincident(g34,g33)
    c: Vertical(g34)
    c: Block(g33)
    c: Coincident(g35,g13)
    c: Coincident(g35,g34)
    c: Horizontal(g35)
    c: Coincident(g36,g13)
    c: Coincident(g36,g20)
    c: Coincident(g37,g20)
    c: Coincident(g37,g30)
    c: Block(g30)
    c: Coincident(g38,g1)
    c: Coincident(g38,g2)
    c: Coincident(g39,g1)
    c: Coincident(g39,g2)
    c: Coincident(g40,g3)
    c: Coincident(g40,g4)
    c: Coincident(g41,g3)
    c: Coincident(g41,g4)
    c: Coincident(g42,g5)
    c: Coincident(g42,g6)
    c: Coincident(g43,g5)
    c: Coincident(g43,g6)
    c: Coincident(g44,g7)
    c: Coincident(g44,g8)
    c: Coincident(g45,g7)
    c: Coincident(g45,g8)
    c: Distance(g30) = 256
    c: Distance(g33) = 100
FEATURE [Part::Extrusion] Extrude002
  Base = -> Sketch001
  Dir = (1,0,0)
  DirMode = 2
  FaceMakerClass = Part::FaceMakerBullseye
  LengthFwd = 8
  LengthRev = 0
  Solid = true
  Symmetric = false
FEATURE [Sketcher::SketchObject] Sketch002
  FullyConstrained = true
  sketch-geometry (20):
    g0: LineSegment StartX=-2.77179 StartY=-200.304 StartZ=0 EndX=5.22821 EndY=-200.304 EndZ=0
    g1: LineSegment StartX=5.22821 StartY=-200.304 StartZ=0 EndX=5.22821 EndY=-197.304 EndZ=0
    g2: LineSegment StartX=-2.77179 StartY=-200.304 StartZ=0 EndX=-2.77179 EndY=-197.304 EndZ=0
    g3: LineSegment StartX=5.22821 StartY=-197.304 StartZ=0 EndX=8.22821 EndY=-197.304 EndZ=0
    g4: LineSegment StartX=-2.77179 StartY=-197.304 StartZ=0 EndX=-5.77179 EndY=-197.304 EndZ=0
    g5: LineSegment StartX=19.2282 StartY=-203.304 StartZ=0 EndX=19.2282 EndY=-206.304 EndZ=0
    g6: LineSegment StartX=-16.7718 StartY=-203.304 StartZ=0 EndX=-16.7718 EndY=-206.304 EndZ=0
    g7: LineSegment StartX=-16.7718 StartY=-206.304 StartZ=0 EndX=19.2282 EndY=-206.304 EndZ=0
    g8: Circle CenterX=-16.7718 CenterY=-203.304 CenterZ=0 NormalX=0 NormalY=0 NormalZ=1 AngleXU=0 Radius=1
    g9: Circle CenterX=-5.77179 CenterY=-203.304 CenterZ=0 NormalX=0 NormalY=0 NormalZ=1 AngleXU=0 Radius=1
    g10: Circle CenterX=-5.77179 CenterY=-197.304 CenterZ=0 NormalX=0 NormalY=0 NormalZ=1 AngleXU=0 Radius=1
    g11: BSplineCurve PolesCount=3 KnotsCount=2 Degree=2 IsPeriodic=0
    g12: GeomPoint X=-16.7718 Y=-203.304 Z=0
    g13: GeomPoint X=-5.77179 Y=-197.304 Z=0
    g14: Circle CenterX=19.2282 CenterY=-203.304 CenterZ=0 NormalX=0 NormalY=0 NormalZ=1 AngleXU=0 Radius=1
    g15: Circle CenterX=8.22821 CenterY=-203.304 CenterZ=0 NormalX=0 NormalY=0 NormalZ=1 AngleXU=0 Radius=1
    g16: Circle CenterX=8.22821 CenterY=-197.304 CenterZ=0 NormalX=0 NormalY=0 NormalZ=1 AngleXU=0 Radius=1
    g17: BSplineCurve PolesCount=3 KnotsCount=2 Degree=2 IsPeriodic=0
    g18: GeomPoint X=19.2282 Y=-203.304 Z=0
    g19: GeomPoint X=8.22821 Y=-197.304 Z=0
  constraints (41):
    c: Horizontal(g0)
    c: Distance(g0) = 8
    c: Coincident(g1,g0)
    c: Vertical(g1)
    c: Distance(g1) = 3
    c: Coincident(g2,g0)
    c: Vertical(g2)
    c: Distance(g2) = 3
    c: Coincident(g3,g1)
    c: Horizontal(g3)
    c: Distance(g3) = 3
    c: Coincident(g4,g2)
    c: Horizontal(g4)
    c: Distance(g4) = 3
    c: Vertical(g5)
    c: Vertical(g6)
    c: Coincident(g7,g6)
    c: Coincident(g7,g5)
    c: Weight(g8) = 1
    c: Equal(g8,g9)
    c: Equal(g8,g10)
    c: Coincident(g11,g4)
    c: InternalAlignment(g8,g11)
    c: InternalAlignment(g9,g11)
    c: InternalAlignment(g10,g11)
    c: InternalAlignment(g12,g11)
    c: InternalAlignment(g13,g11)
    c: Coincident(g17,g5)
    c: Weight(g14) = 1
    c: Equal(g14,g15)
    c: Equal(g14,g16)
    c: Coincident(g17,g3)
    c: InternalAlignment(g14,g17)
    c: InternalAlignment(g15,g17)
    c: InternalAlignment(g16,g17)
    c: InternalAlignment(g18,g17)
    c: InternalAlignment(g19,g17)
    c: Block(g7)
    c: Block(g17)
    c: Block(g11)
    c: Block(g6)
FEATURE [Part::Extrusion] Extrude003
  Base = -> Sketch002
  Dir = (0,0,1)
  DirMode = 2
  FaceMakerClass = Part::FaceMakerBullseye
  LengthFwd = 260
  LengthRev = 0
  Solid = true
  Symmetric = false
FEATURE [Part::Extrusion] Extrude
  Base = -> Sketch
  Dir = (0,0,1)
  DirMode = 2
  FaceMakerClass = Part::FaceMakerBullseye
  LengthFwd = 14
  LengthRev = 0
  Solid = true
  Symmetric = false
